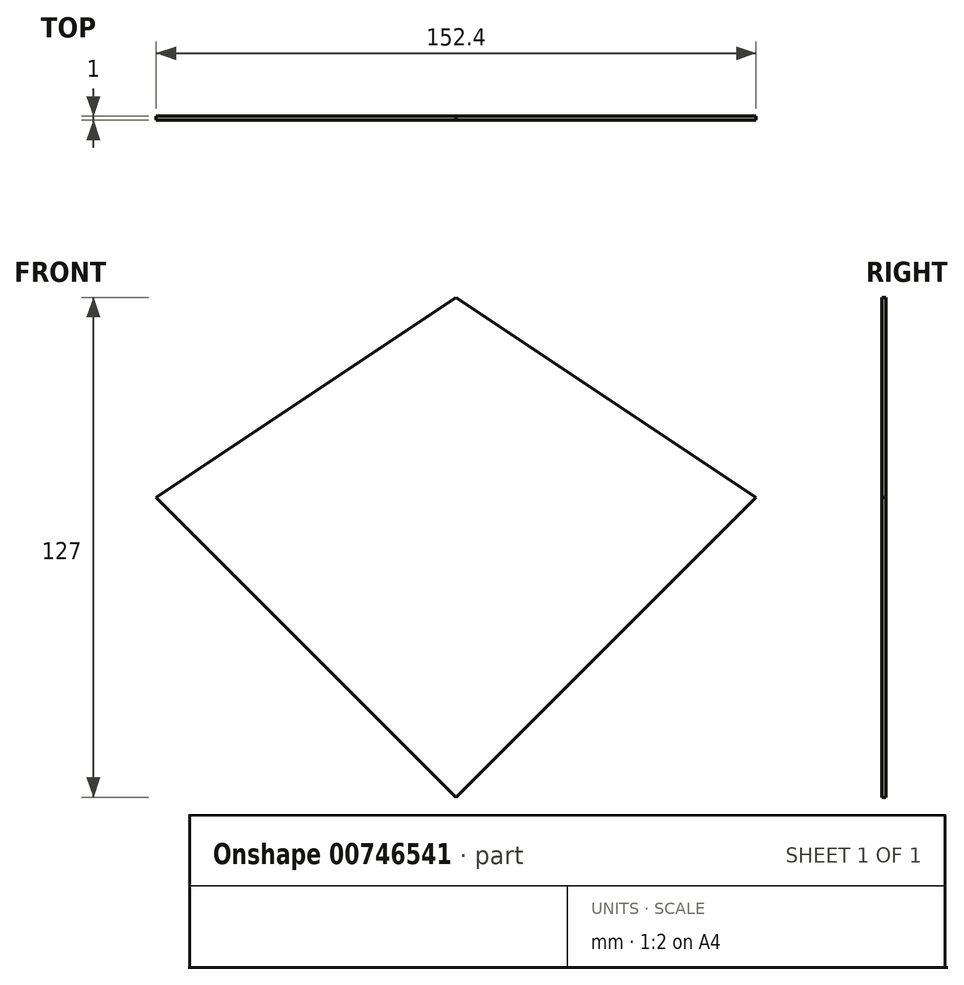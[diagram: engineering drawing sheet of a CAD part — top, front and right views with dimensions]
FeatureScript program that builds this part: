
annotation { "Feature Type Name" : "Feature", "Feature Type Description" : "" }
export const myFeature = defineFeature(function(context is Context, id is Id, definition is map)
    precondition{}
    {
        {
            var Q0;
            Q0=qCreatedBy(makeId("Front.planeOp"),FACE);
            var sketch = newSketch(context, id + "F0", { "sketchPlane" : qUnion([Q0])});
            skLineSegment(sketch, "E0", {"start": v(0, 0) * mm, "end": v(76.2, 0) * mm});
            skLineSegment(sketch, "E1", {"start": v(0, 0) * mm, "end": v(-76.2, 0) * mm});
            skLineSegment(sketch, "E2", {"start": v(0, 0) * mm, "end": v(0, 50.8) * mm});
            skLineSegment(sketch, "E3", {"start": v(0, 0) * mm, "end": v(0, -76.2) * mm});
            skLineSegment(sketch, "E4", {"start": v(0, 50.8) * mm, "end": v(76.2, 0) * mm});
            skLineSegment(sketch, "E5", {"start": v(-76.2, 0) * mm, "end": v(0, 50.8) * mm});
            skLineSegment(sketch, "E6", {"start": v(-76.2, 0) * mm, "end": v(0, -76.2) * mm});
            skLineSegment(sketch, "E7", {"start": v(0, -76.2) * mm, "end": v(76.2, 0) * mm});
            skSolve(sketch);
        }
        {
            var Q0;
            Q0 = qSketchRegion(id + "F0", true);
            extrude(context, id + "F1", {"entities" : qUnion([Q0]), "depth" : 1 * mm, "offsetDistance" : 25.4 * mm});
        }
    });
